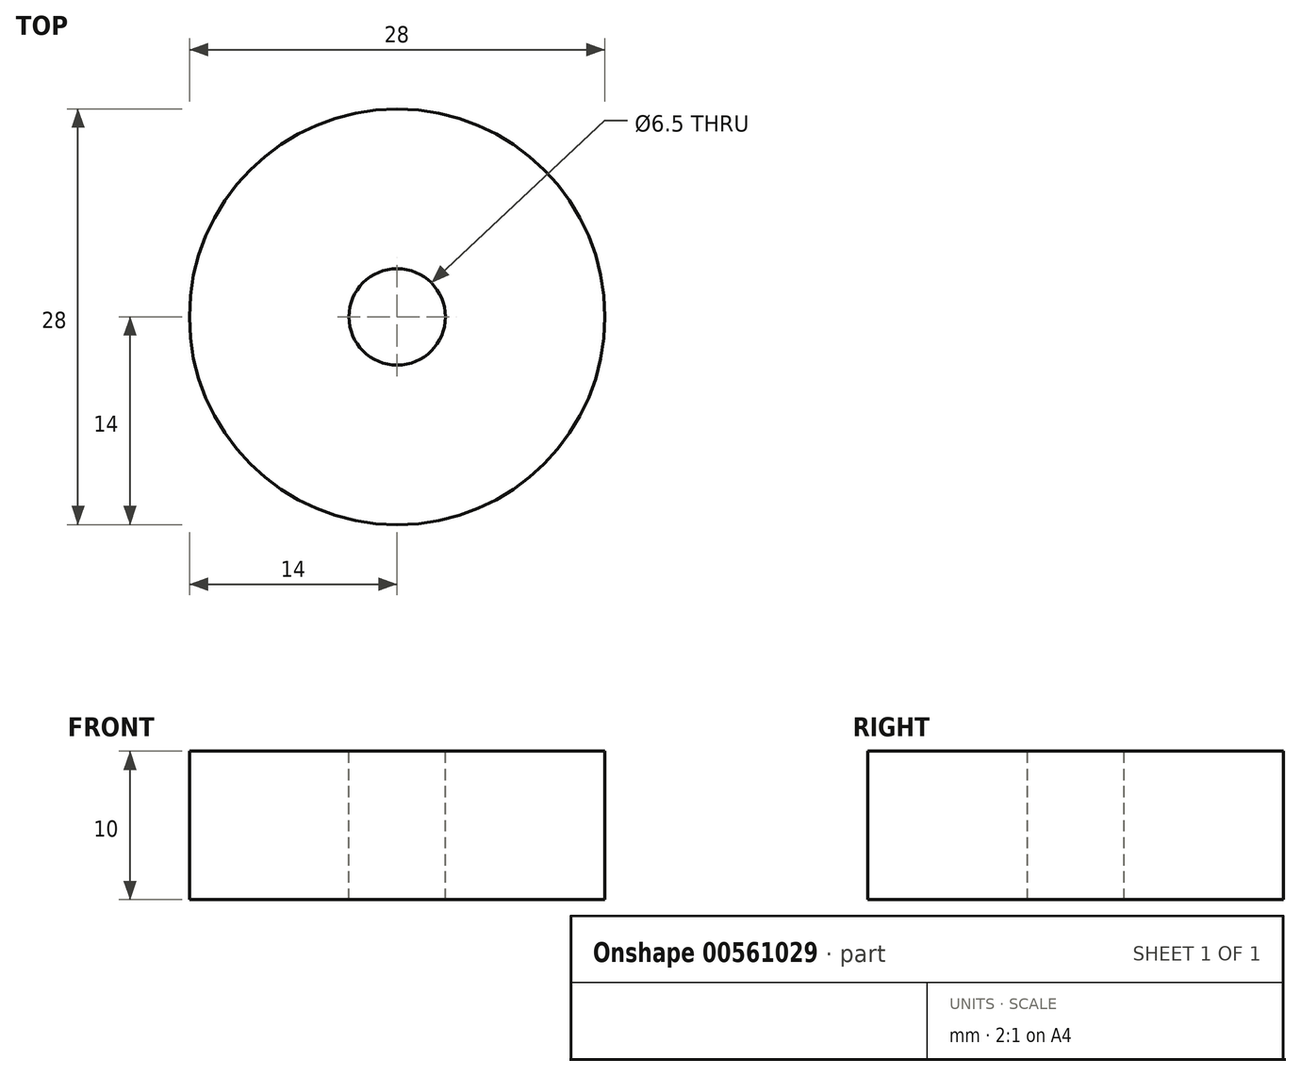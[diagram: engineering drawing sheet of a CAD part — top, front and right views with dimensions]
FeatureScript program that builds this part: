
annotation { "Feature Type Name" : "Feature", "Feature Type Description" : "" }
export const myFeature = defineFeature(function(context is Context, id is Id, definition is map)
    precondition{}
    {
        {
            var Q0;
            Q0=qCreatedBy(makeId("Top.planeOp"),FACE);
            var sketch = newSketch(context, id + "F0", { "sketchPlane" : qUnion([Q0])});
            skCircle(sketch, "E0", {"center": v(0, 0) * mm, "radius": 14 * mm});
            skSolve(sketch);
        }
        {
            var Q0;
            Q0=qSketchRegion(id+"F0",true);
            extrude(context, id + "F1", {"entities" : qUnion([Q0]), "depth" : 10 * mm, "offsetDistance" : 25 * mm});
        }
        {
            var Q0;
            Q0=makeQuery(id+"F1.opExtrude","CAP_FACE",FACE,{"disambiguationData":[OSD([sQuery(id+"F0.wireOp",EDGE,"E0")])],"isStart":false});
            var sketch = newSketch(context, id + "F2", { "sketchPlane" : qUnion([Q0])});
            skCircle(sketch, "E1", {"center": v(0, 0) * mm, "radius": 3.25 * mm});
            skSolve(sketch);
        }
        {
            var Q0;
            Q0=makeQuery(id+"F2.imprint","IMPRINT",FACE,{"disambiguationData":[TD([[makeQuery(id+"F2.imprint","IMPRINT",EDGE,{"derivedFrom":sQuery(id+"F2.wireOp",EDGE,"E1")}),1.0]])]});
            extrude(context, id + "F3", {"entities" : qUnion([Q0]), "operationType" : NewBodyOperationType.REMOVE, "oppositeDirection" : true, "depth" : 25 * mm, "offsetDistance" : 25 * mm});
        }
    });
